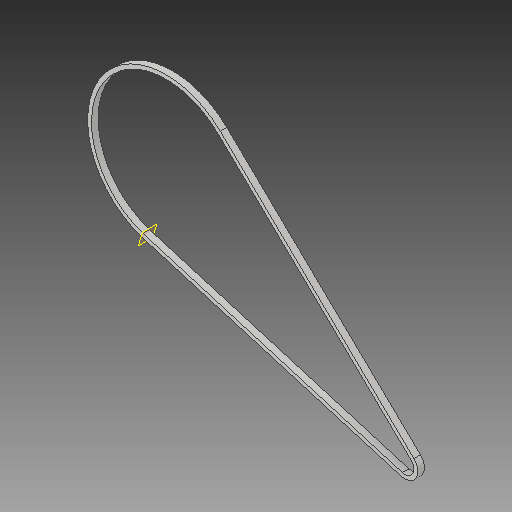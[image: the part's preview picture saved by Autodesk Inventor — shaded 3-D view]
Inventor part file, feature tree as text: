
AUTODESK INVENTOR PART (.ipt)
format: ipt  version: 2019.2 (Build 232265000, 265)  size: 119,296 bytes
history: native  units: mm
features: plane x2, sketch x1, sweep x1
ambient origin geometry x8: Origin, YZ Plane, XZ Plane, XY Plane, X Axis, Y Axis, Z Axis, Center Point
bodies: Solid1 (feature_tree)
feature tree (4):
  plane  "Work Plane6"
  sketch  "Sketch1"  dims[d0=6.0mm d1=10.0mm d2=0.0mm d3=0.0mm]
  plane  "Work Plane13"
  sweep  "Sweep1"
